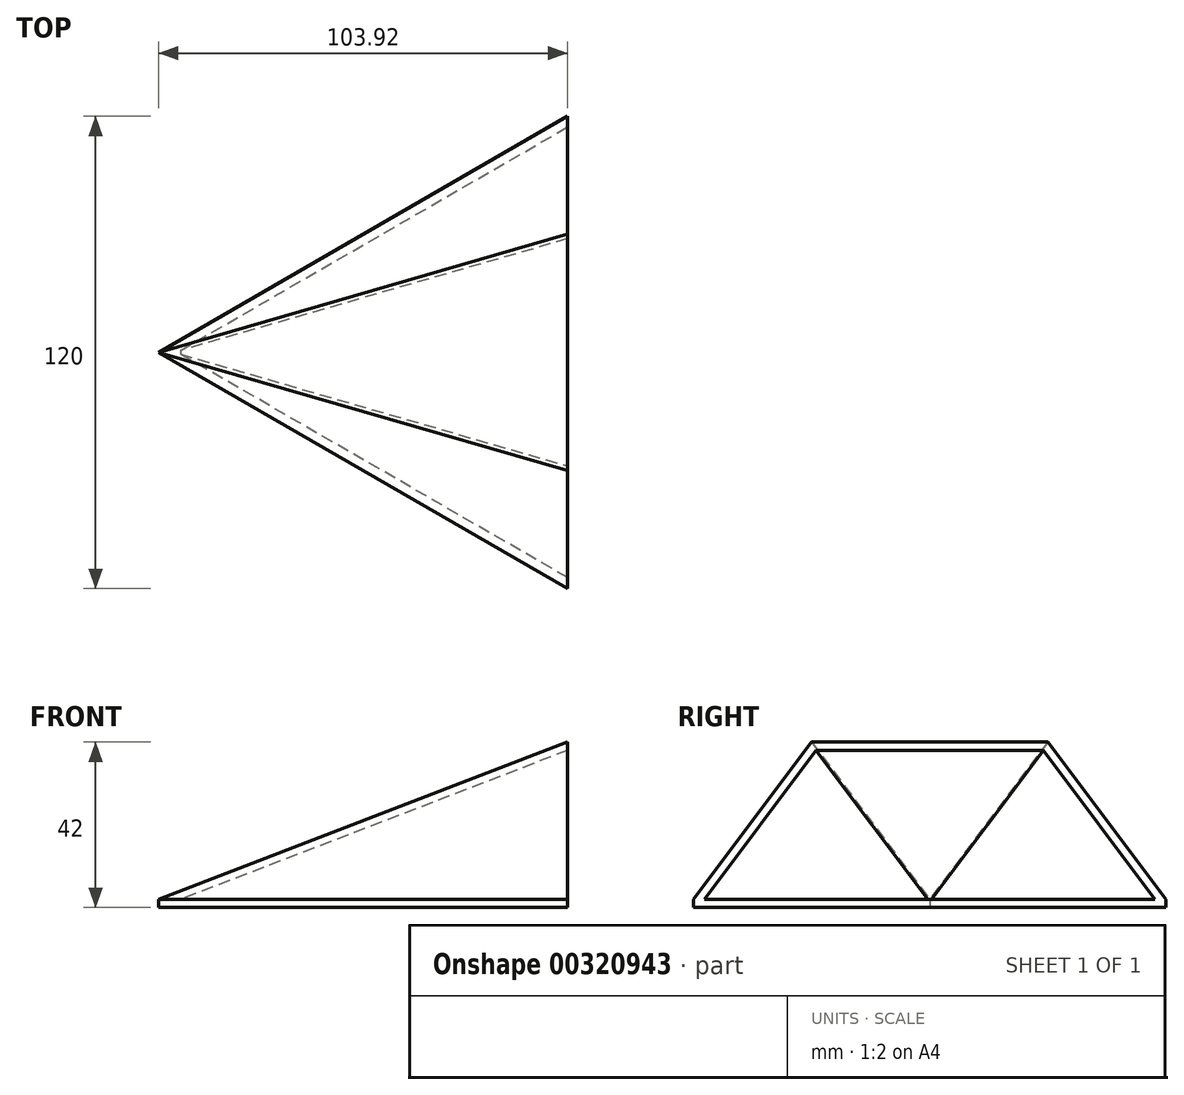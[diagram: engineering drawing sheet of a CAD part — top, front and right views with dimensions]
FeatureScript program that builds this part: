
annotation { "Feature Type Name" : "Feature", "Feature Type Description" : "" }
export const myFeature = defineFeature(function(context is Context, id is Id, definition is map)
    precondition{}
    {
        {
            var Q0;
            Q0=qCreatedBy(makeId("Top.planeOp"),FACE);
            var sketch = newSketch(context, id + "F0", { "sketchPlane" : qUnion([Q0])});
            skCircle(sketch, "E0.cCircle", {"center": v(0, 0) * mm, "radius": 34.64 * mm, "construction": true});
            skLineSegment(sketch, "E0.0", {"start": v(34.64, 60) * mm, "end": v(34.64, -60) * mm});
            skLineSegment(sketch, "E0.1", {"start": v(34.64, -60) * mm, "end": v(-69.28, 0) * mm});
            skLineSegment(sketch, "E0.2", {"start": v(-69.28, 0) * mm, "end": v(34.64, 60) * mm});
            skPoint(sketch, "E0.0.midPoint", {"position": v(34.64, 0) * mm});
            skSolve(sketch);
        }
        {
            var Q0;
            Q0=makeQuery(id+"F0.imprint","IMPRINT",FACE,{"disambiguationData":[TD([[makeQuery(id+"F0.imprint","IMPRINT",EDGE,{"derivedFrom":sQuery(id+"F0.wireOp",EDGE,"E0.0")}),-1.0]])]});
            extrude(context, id + "F1", {"entities" : qUnion([Q0]), "depth" : 2 * mm});
        }
        {
            var Q0;
            Q0=makeQuery(id+"F1.opExtrude","SWEPT_FACE",FACE,{"disambiguationData":[OSD([sQuery(id+"F0.wireOp",EDGE,"E0.0")])]});
            var sketch = newSketch(context, id + "F2", { "sketchPlane" : qUnion([Q0])});
            skLineSegment(sketch, "E1", {"start": v(30, 42) * mm, "end": v(60, 2) * mm});
            skPoint(sketch, "E2.endSnap0", {"position": v(0, 2) * mm});
            skLineSegment(sketch, "E3", {"start": v(30, 42) * mm, "end": v(0, 42) * mm});
            skPoint(sketch, "E4.orphan", {"position": v(0, 59.43) * mm});
            skPoint(sketch, "E2.start.orphan", {"position": v(0, 2) * mm});
            skLineSegment(sketch, "E5", {"start": v(0, 42) * mm, "end": v(0, 84.86) * mm, "construction": true});
            skLineSegment(sketch, "E6.MirrorCS", {"start": v(-30, 42) * mm, "end": v(0, 42) * mm});
            skLineSegment(sketch, "E7.MirrorCS", {"start": v(-30, 42) * mm, "end": v(-60, 2) * mm});
            skLineSegment(sketch, "E8", {"start": v(60, 2) * mm, "end": v(-60, 2) * mm});
            skSolve(sketch);
        }
        {
            var Q1;
            Q1=makeQuery(id+"F2.imprint","IMPRINT",FACE,{"disambiguationData":[TD([[makeQuery(id+"F2.imprint","IMPRINT",EDGE,{"derivedFrom":sQuery(id+"F2.wireOp",EDGE,"E1")}),-1.0]])]});
            var Q2;
            Q2=makeQuery(id+"F1.opExtrude","CAP_VERTEX",VERTEX,{"disambiguationData":[OSD([sQuery(id+"F0.wireOp",EDGE,"E0.1"),sQuery(id+"F0.wireOp",EDGE,"E0.2")])],"isStart":false});
            loft(context, id + "F3", {"operationType" : NewBodyOperationType.ADD, "sheetProfilesArray" : [{ "sheetProfileEntities" : qUnion([Q1]) }, { "sheetProfileEntities" : qUnion([Q2]) }]});
        }
        {
            var Q0;
            Q0=makeQuery(id+"F3.boolean.opBoolean","MERGE",FACE,{"derivedFrom":[makeQuery(id+"F1.opExtrude","SWEPT_FACE",FACE,{"disambiguationData":[OSD([sQuery(id+"F0.wireOp",EDGE,"E0.0")])]}),makeQuery(id+"F3.opLoft","CAP_FACE",FACE,{"disambiguationData":[OSD([makeQuery(id+"F2.imprint","IMPRINT",FACE,{"disambiguationData":[TD([[makeQuery(id+"F2.imprint","IMPRINT",EDGE,{"derivedFrom":sQuery(id+"F2.wireOp",EDGE,"E1")}),-1.0]])]})])],"isStart":true})]});
            shell(context, id + "F4", {"entities" : qUnion([Q0]), "thickness" : 2 * mm});
        }
        {
            var Q0;
            Q0=qCreatedBy(makeId("Right.planeOp"),FACE);
            cPlane(context, id + "F5", {"entities" : qUnion([Q0]), "cplaneType" : CPlaneType.OFFSET, "offset" : 56.6 * mm, "oppositeDirection" : true, "width" : 150 * mm, "height" : 150 * mm});
        }
    });
